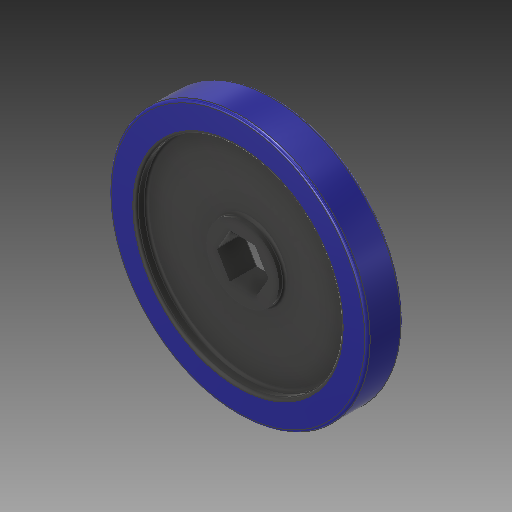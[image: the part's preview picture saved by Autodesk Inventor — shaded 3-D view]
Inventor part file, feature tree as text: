
AUTODESK INVENTOR PART (.ipt)
format: ipt  version: 2017 (Build 210142000, 142)  size: 218,112 bytes
history: native  units: in
note: dims shown in document units (in); Inventor stores cm internally (conversion verified against a paired STEP export)
features: extrude x4, sketch x4, fillet x1, projected_geometry x1
ambient origin geometry x8: Origin, YZ Plane, XZ Plane, XY Plane, X Axis, Y Axis, Z Axis, Center Point
bodies: Solid1 (feature_tree)
feature tree (10):
  extrude  "Extrusion1"  Depth=0.15in TaperAngle=0.0deg
  extrude  "Extrusion2"  Depth=0.4in TaperAngle=0.0deg
  extrude  "Extrusion3"  Depth=0.3in TaperAngle=0.0deg
  extrude  "Extrusion4"  Depth=0.3in TaperAngle=0.0deg
  fillet  "Fillet1"  Radius=0.03in
  sketch  "Sketch1"  dims[d0=2.875in d1=0.15in d2=0.0in]
  sketch  "Sketch2"  dims[d3=2.275in d4=0.4in d5=0.0in]
  projected_geometry  "Projected Loop1"
  sketch  "Sketch3"  dims[d6=0.8in d7=0.3in d8=0.0in]
  sketch  "Sketch4"  dims[d9=0.5in d10=0.3in d11=0.0in d12=0.03in]
